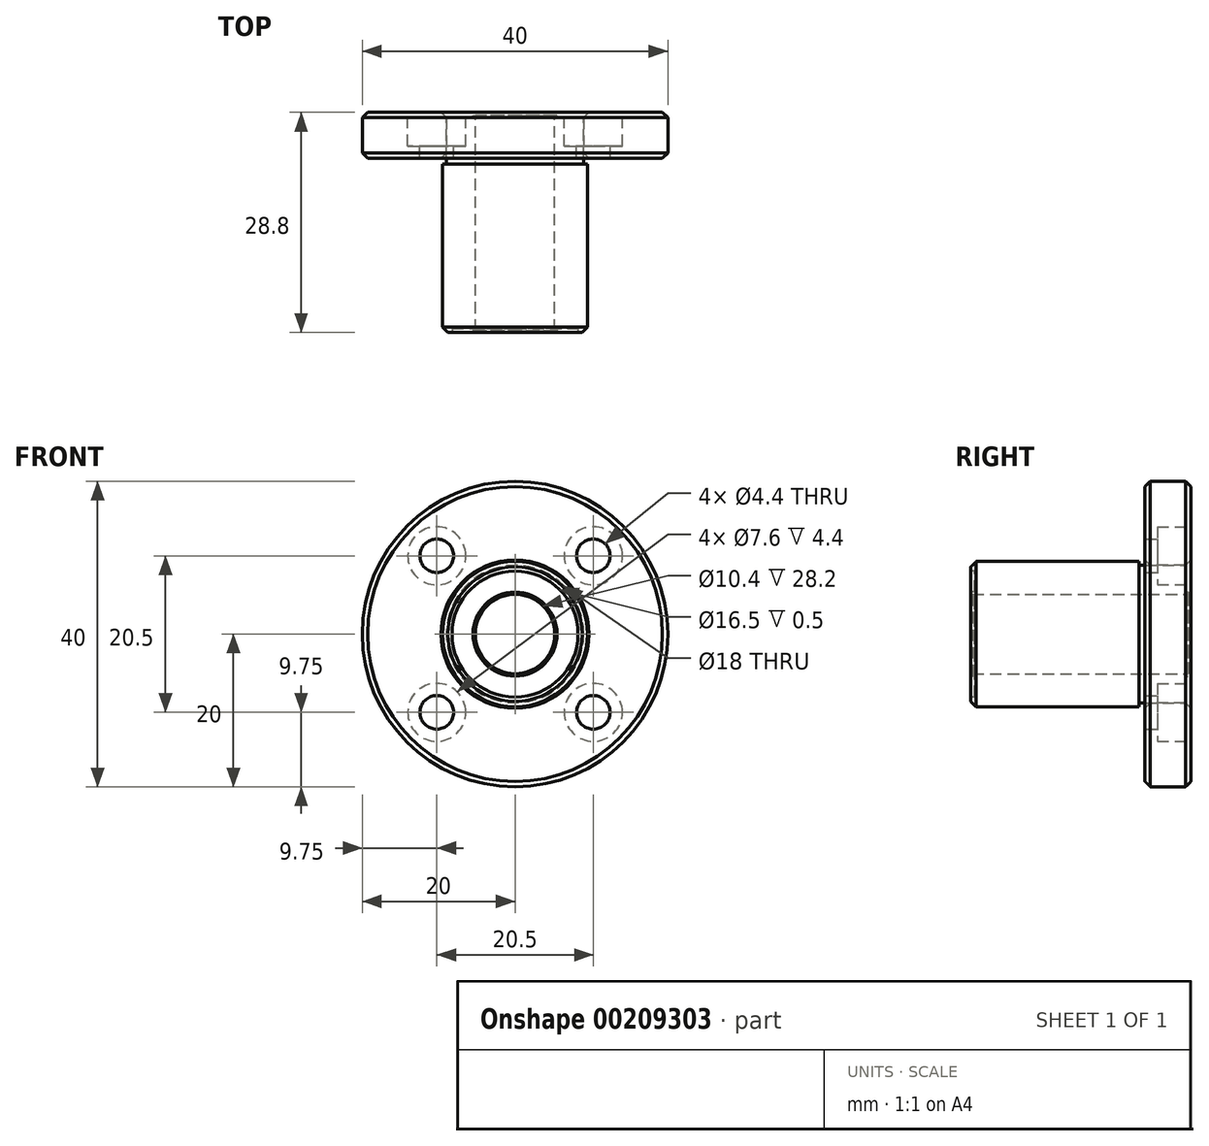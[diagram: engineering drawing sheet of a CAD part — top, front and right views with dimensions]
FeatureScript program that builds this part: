
annotation { "Feature Type Name" : "Feature", "Feature Type Description" : "" }
export const myFeature = defineFeature(function(context is Context, id is Id, definition is map)
    precondition{}
    {
        {
            var Q0;
            Q0=qCreatedBy(makeId("Front.planeOp"),FACE);
            var sketch = newSketch(context, id + "F0", { "sketchPlane" : qUnion([Q0])});
            skCircle(sketch, "E0", {"center": v(0, 0) * mm, "radius": 20 * mm});
            skCircle(sketch, "E1", {"center": v(0, 0) * mm, "radius": 9 * mm});
            skSolve(sketch);
        }
        {
            var Q0;
            Q0=makeQuery(id+"F0.imprint","IMPRINT",FACE,{"disambiguationData":[TD([[makeQuery(id+"F0.imprint","IMPRINT",EDGE,{"derivedFrom":sQuery(id+"F0.wireOp",EDGE,"E0")}),1.0]])]});
            extrude(context, id + "F1", {"entities" : qUnion([Q0]), "oppositeDirection" : true, "depth" : 6 * mm});
        }
        {
            var Q0;
            Q0=qCreatedBy(makeId("Top.planeOp"),FACE);
            var sketch = newSketch(context, id + "F2", { "sketchPlane" : qUnion([Q0])});
            skLineSegment(sketch, "E2", {"start": v(0, 6) * mm, "end": v(0, -22.8) * mm});
            skLineSegment(sketch, "E3", {"start": v(0, -22.8) * mm, "end": v(-9.5, -22.8) * mm});
            skLineSegment(sketch, "E4", {"start": v(-9.5, -22.8) * mm, "end": v(-9.5, -0.8) * mm});
            skLineSegment(sketch, "E5", {"start": v(-9.5, -0.8) * mm, "end": v(-9, -0.8) * mm});
            skLineSegment(sketch, "E6", {"start": v(-9, -0.8) * mm, "end": v(-9, 6) * mm});
            skLineSegment(sketch, "E7", {"start": v(-9, 6) * mm, "end": v(0, 6) * mm});
            skLineSegment(sketch, "E8", {"start": v(0, 24.72) * mm, "end": v(0, 6) * mm, "construction": true});
            skSolve(sketch);
        }
        {
            var Q0;
            Q0=makeQuery(id+"F2.imprint","IMPRINT",FACE,{"disambiguationData":[TD([[makeQuery(id+"F2.imprint","IMPRINT",EDGE,{"derivedFrom":sQuery(id+"F2.wireOp",EDGE,"E2")}),-1.0]])]});
            var Q1;
            Q1=sQuery(id+"F2.wireOp",EDGE,"E8");
            revolve(context, id + "F3", {"entities" : qUnion([Q0]), "axis" : qUnion([Q1]), "revolveType" : RevolveType.FULL});
        }
        {
            var Q0;
            Q0=makeQuery(id+"F1.opExtrude","SWEPT_FACE",FACE,{"disambiguationData":[OSD([sQuery(id+"F0.wireOp",EDGE,"E0")])]});
            var Q1;
            Q1=makeQuery(id+"F1.opExtrude","SWEPT_FACE",FACE,{"disambiguationData":[OSD([sQuery(id+"F0.wireOp",EDGE,"E1")])]});
            chamfer(context, id + "F4", {"entities" : qUnion([Q0, Q1]), "width" : .7 * mm, "tangentPropagation" : true});
        }
        {
            var Q0;
            Q0=makeQuery(id+"F1.opExtrude","CAP_FACE",FACE,{"disambiguationData":[OSD([sQuery(id+"F0.wireOp",EDGE,"E0"),sQuery(id+"F0.wireOp",EDGE,"E1")])],"isStart":false});
            var sketch = newSketch(context, id + "F5", { "sketchPlane" : qUnion([Q0])});
            skLineSegment(sketch, "E9.bottom", {"start": v(-10.25, 10.25) * mm, "end": v(10.25, 10.25) * mm});
            skLineSegment(sketch, "E9.top", {"start": v(-10.25, -10.25) * mm, "end": v(10.25, -10.25) * mm});
            skLineSegment(sketch, "E9.left", {"start": v(-10.25, 10.25) * mm, "end": v(-10.25, -10.25) * mm});
            skLineSegment(sketch, "E9.right", {"start": v(10.25, 10.25) * mm, "end": v(10.25, -10.25) * mm});
            skLineSegment(sketch, "E10", {"start": v(-10.25, 10.25) * mm, "end": v(10.25, -10.25) * mm});
            skSolve(sketch);
        }
        {
            var Q0;
            Q0=sQuery(id+"F5.wireOp",VERTEX,"E9.left.start");
            var Q1;
            Q1=sQuery(id+"F5.wireOp",VERTEX,"E9.bottom.end");
            var Q2;
            Q2=sQuery(id+"F5.wireOp",VERTEX,"E9.top.end");
            var Q3;
            Q3=sQuery(id+"F5.wireOp",VERTEX,"E9.left.end");
            var Q4;
            Q4=makeQuery(id+"F1.opExtrude","SWEPT_BODY",BODY,{"disambiguationData":[OSD([sQuery(id+"F0.wireOp",EDGE,"E0"),sQuery(id+"F0.wireOp",EDGE,"E1")])]});
            hole(context, id + "F6", {"style" : HoleStyle.C_BORE, "endStyle" : HoleEndStyle.THROUGH, "holeDiameter" : 4.4 * mm, "cBoreDiameter" : 7.6 * mm, "cBoreDepth" : 4.4 * mm, "locations" : qUnion([Q0, Q1, Q2, Q3]), "scope" : qUnion([Q4]), "isTappedThrough" : true});
        }
        {
            var Q0;
            Q0=makeQuery(id+"F3.opRevolve","SWEPT_EDGE",EDGE,{"disambiguationData":[OSD([sQuery(id+"F2.wireOp",EDGE,"E3"),sQuery(id+"F2.wireOp",EDGE,"E4")])]});
            chamfer(context, id + "F7", {"entities" : qUnion([Q0]), "width" : .7 * mm, "tangentPropagation" : true});
        }
        {
            var Q0;
            Q0=makeQuery(id+"F3.opRevolve","SWEPT_FACE",FACE,{"disambiguationData":[OSD([sQuery(id+"F2.wireOp",EDGE,"E7")])]});
            var sketch = newSketch(context, id + "F8", { "sketchPlane" : qUnion([Q0])});
            skCircle(sketch, "E11", {"center": v(0, 0) * mm, "radius": 9 * mm});
            skCircle(sketch, "E12", {"center": v(0, 0) * mm, "radius": 5.5 * mm});
            skCircle(sketch, "E13", {"center": v(0, 0) * mm, "radius": 5.2 * mm});
            skSolve(sketch);
        }
        {
            var Q0;
            Q0=makeQuery(id+"F8.imprint","IMPRINT",FACE,{"disambiguationData":[TD([[makeQuery(id+"F8.imprint","IMPRINT",EDGE,{"derivedFrom":sQuery(id+"F8.wireOp",EDGE,"E11")}),1.0]])]});
            extrude(context, id + "F9", {"entities" : qUnion([Q0]), "operationType" : NewBodyOperationType.REMOVE, "oppositeDirection" : true, "depth" : .7 * mm});
        }
        {
            var Q0;
            Q0=makeQuery(id+"F8.imprint","IMPRINT",FACE,{"disambiguationData":[TD([[makeQuery(id+"F8.imprint","IMPRINT",EDGE,{"derivedFrom":sQuery(id+"F8.wireOp",EDGE,"E12")}),1.0]])]});
            extrude(context, id + "F10", {"entities" : qUnion([Q0]), "operationType" : NewBodyOperationType.REMOVE, "oppositeDirection" : true, "depth" : .4 * mm});
        }
        {
            var Q0;
            Q0=makeQuery(id+"F8.imprint","IMPRINT",FACE,{"disambiguationData":[TD([[makeQuery(id+"F8.imprint","IMPRINT",EDGE,{"derivedFrom":sQuery(id+"F8.wireOp",EDGE,"E13")}),1.0]])]});
            extrude(context, id + "F11", {"entities" : qUnion([Q0]), "operationType" : NewBodyOperationType.REMOVE, "endBound" : BoundingType.UP_TO_NEXT, "oppositeDirection" : true, "depth" : 25 * mm});
        }
        {
            var Q0;
            Q0=makeQuery(id+"F3.opRevolve","SWEPT_FACE",FACE,{"disambiguationData":[OSD([sQuery(id+"F2.wireOp",EDGE,"E3")])]});
            var sketch = newSketch(context, id + "F12", { "sketchPlane" : qUnion([Q0])});
            skCircle(sketch, "E14", {"center": v(0, 0) * mm, "radius": 8.25 * mm});
            skCircle(sketch, "E15", {"center": v(0, 0) * mm, "radius": 5.5 * mm});
            skCircle(sketch, "E16", {"center": v(0, 0) * mm, "radius": 5.2 * mm});
            skSolve(sketch);
        }
        {
            var Q0;
            Q0=makeQuery(id+"F12.imprint","IMPRINT",FACE,{"disambiguationData":[TD([[makeQuery(id+"F12.imprint","IMPRINT",EDGE,{"derivedFrom":sQuery(id+"F12.wireOp",EDGE,"E14")}),1.0]])]});
            extrude(context, id + "F13", {"entities" : qUnion([Q0]), "operationType" : NewBodyOperationType.REMOVE, "oppositeDirection" : true, "depth" : .5 * mm});
        }
        {
            var Q0;
            Q0=makeQuery(id+"F12.imprint","IMPRINT",FACE,{"disambiguationData":[TD([[makeQuery(id+"F12.imprint","IMPRINT",EDGE,{"derivedFrom":sQuery(id+"F12.wireOp",EDGE,"E15")}),1.0]])]});
            extrude(context, id + "F14", {"entities" : qUnion([Q0]), "operationType" : NewBodyOperationType.REMOVE, "oppositeDirection" : true, "depth" : .2 * mm});
        }
    });
